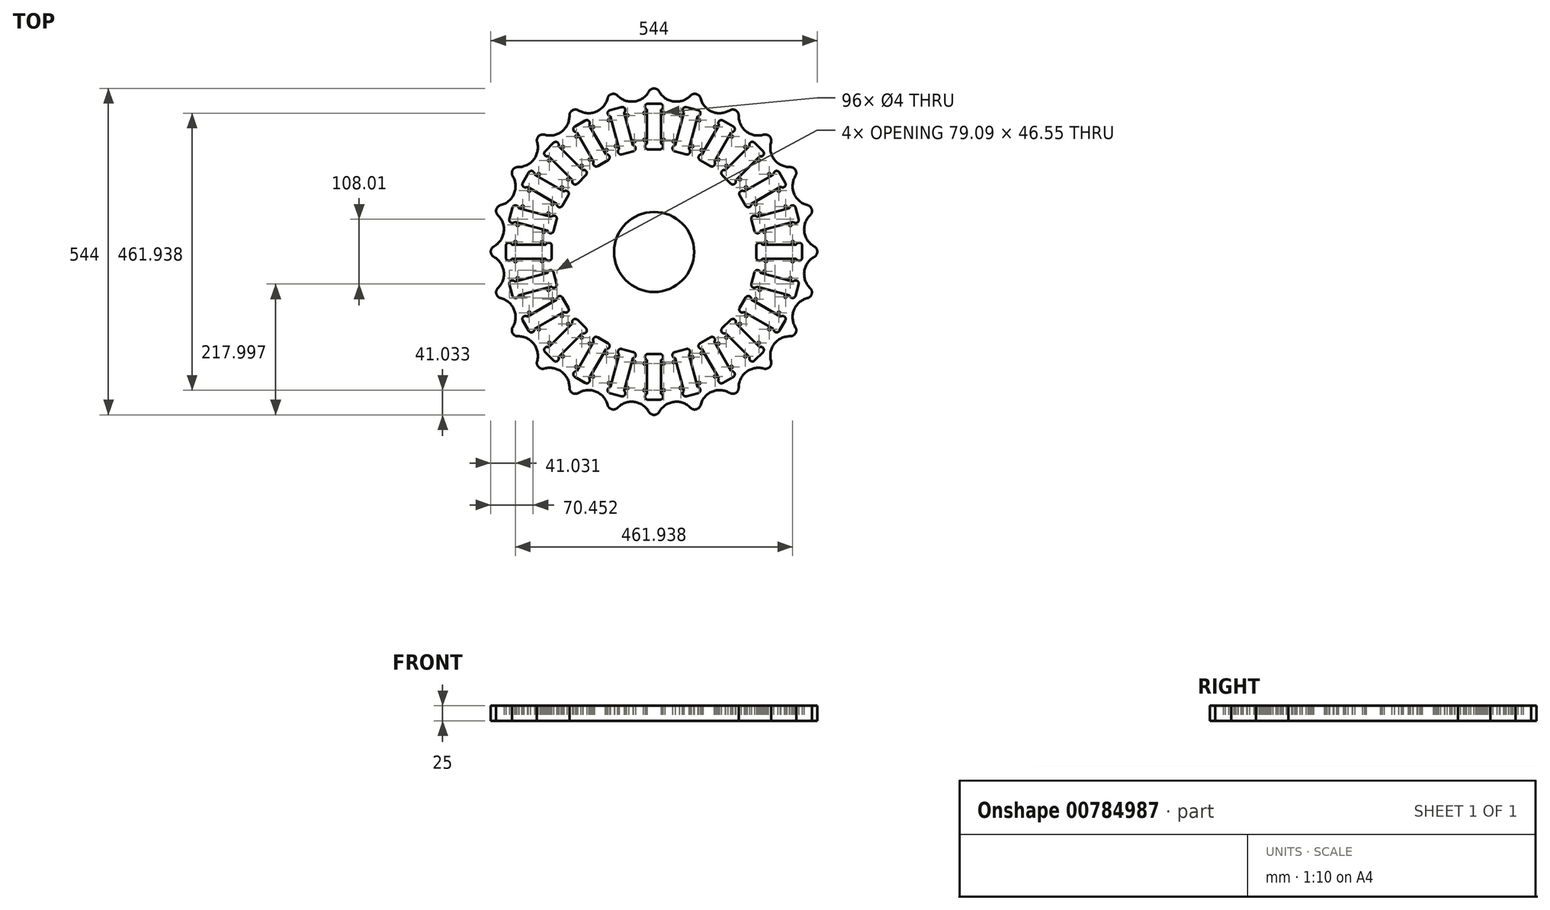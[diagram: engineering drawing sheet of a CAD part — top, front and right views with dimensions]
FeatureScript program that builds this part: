
annotation { "Feature Type Name" : "Feature", "Feature Type Description" : "" }
export const myFeature = defineFeature(function(context is Context, id is Id, definition is map)
    precondition{}
    {
        {
            var Q0;
            Q0=qCreatedBy(makeId("Top.planeOp"),FACE);
            var sketch = newSketch(context, id + "F0", { "sketchPlane" : qUnion([Q0])});
            skCircle(sketch, "E0", {"center": v(0, 0) * mm, "radius": 66.68 * mm});
            skCircle(sketch, "E1", {"center": v(0, 0) * mm, "radius": 35 * mm, "construction": true});
            skArc(sketch, "E2", {"start": v(-21.4, 32.9) * mm, "mid": v(-22.65, 27.02) * mm, "end": v(-16.77, 25.78) * mm});
            skArc(sketch, "E3", {"start": v(16.77, 25.78) * mm, "mid": v(22.65, 27.02) * mm, "end": v(21.4, 32.9) * mm});
            skArc(sketch, "E4", {"start": v(16.77, 25.78) * mm, "mid": v(0, 30.75) * mm, "end": v(-16.77, 25.78) * mm});
            skArc(sketch, "E5", {"start": v(21.4, 32.9) * mm, "mid": v(0, 39.25) * mm, "end": v(-21.4, 32.9) * mm});
            skPoint(sketch, "E6", {"position": v(0, 30.75) * mm});
            skPoint(sketch, "E7", {"position": v(-22.5, 26.8) * mm});
            skPoint(sketch, "E8", {"position": v(22.5, 26.8) * mm});
            skCircle(sketch, "E9", {"center": v(0, 0) * mm, "radius": 22.23 * mm});
            skArc(sketch, "E10.1.0", {"start": v(-17.8, -34.99) * mm, "mid": v(-12.08, -33.12) * mm, "end": v(-13.94, -27.4) * mm});
            skArc(sketch, "E10.1.1", {"start": v(-39.2, 2.08) * mm, "mid": v(-34, -19.62) * mm, "end": v(-17.8, -34.99) * mm});
            skArc(sketch, "E10.1.2", {"start": v(-30.7, 1.63) * mm, "mid": v(-26.63, -15.37) * mm, "end": v(-13.94, -27.4) * mm});
            skArc(sketch, "E10.1.3", {"start": v(-30.7, 1.63) * mm, "mid": v(-34.72, 6.1) * mm, "end": v(-39.2, 2.08) * mm});
            skArc(sketch, "E10.2.0", {"start": v(39.2, 2.08) * mm, "mid": v(34.72, 6.1) * mm, "end": v(30.7, 1.63) * mm});
            skArc(sketch, "E10.2.1", {"start": v(17.8, -34.99) * mm, "mid": v(34, -19.63) * mm, "end": v(39.2, 2.08) * mm});
            skArc(sketch, "E10.2.2", {"start": v(13.94, -27.4) * mm, "mid": v(26.63, -15.38) * mm, "end": v(30.7, 1.63) * mm});
            skArc(sketch, "E10.2.3", {"start": v(13.94, -27.4) * mm, "mid": v(12.08, -33.12) * mm, "end": v(17.8, -34.99) * mm});
            skLineSegment(sketch, "E11", {"start": v(0, 0) * mm, "end": v(0, 283.97) * mm, "construction": true});
            skArc(sketch, "E12", {"start": v(8.75, 267.34) * mm, "mid": v(0, 272.5) * mm, "end": v(-8.75, 267.34) * mm});
            skLineSegment(sketch, "E13", {"start": v(0, 0) * mm, "end": v(37.8, 287.62) * mm, "construction": true});
            skArc(sketch, "E14", {"start": v(8.75, 267.34) * mm, "mid": v(18.9, 256.2) * mm, "end": v(32.96, 250.84) * mm});
            skPoint(sketch, "E15", {"position": v(32.96, 250.84) * mm});
            skArc(sketch, "E16.MirrorC", {"start": v(-8.75, 267.34) * mm, "mid": v(-18.9, 256.2) * mm, "end": v(-32.96, 250.84) * mm});
            skLineSegment(sketch, "E17.MirrorCS", {"start": v(0, 0) * mm, "end": v(-37.8, 287.62) * mm, "construction": true});
            skLineSegment(sketch, "E18", {"start": v(-10, 247.26) * mm, "end": v(0, 247.26) * mm});
            skLineSegment(sketch, "E19", {"start": v(-10, 171.06) * mm, "end": v(0, 171.06) * mm});
            skArc(sketch, "E20", {"start": v(-10, 247.26) * mm, "mid": v(-14.99, 243.15) * mm, "end": v(-11.9, 237.47) * mm});
            skPoint(sketch, "E21", {"position": v(-10, 247.26) * mm});
            skArc(sketch, "E22", {"start": v(-11.9, 180.85) * mm, "mid": v(-14.99, 175.17) * mm, "end": v(-10, 171.06) * mm});
            skPoint(sketch, "E23", {"position": v(-10, 171.06) * mm});
            skLineSegment(sketch, "E24", {"start": v(-11.9, 237.47) * mm, "end": v(-11.9, 180.85) * mm});
            skPoint(sketch, "E25", {"position": v(-15.08, 242.18) * mm});
            skPoint(sketch, "E26", {"position": v(-15.08, 176.14) * mm});
            skLineSegment(sketch, "E27.MirrorCS", {"start": v(10, 247.26) * mm, "end": v(0, 247.26) * mm});
            skArc(sketch, "E28.MirrorCS", {"start": v(10, 247.26) * mm, "mid": v(14.99, 243.15) * mm, "end": v(11.9, 237.47) * mm});
            skLineSegment(sketch, "E29.MirrorCS", {"start": v(11.9, 237.47) * mm, "end": v(11.9, 180.85) * mm});
            skArc(sketch, "E30.MirrorCS", {"start": v(11.9, 180.85) * mm, "mid": v(14.99, 175.17) * mm, "end": v(10, 171.06) * mm});
            skLineSegment(sketch, "E31.MirrorCS", {"start": v(10, 171.06) * mm, "end": v(0, 171.06) * mm});
            skCircle(sketch, "E32", {"center": v(-15.9, 231.47) * mm, "radius": 2 * mm});
            skCircle(sketch, "E33", {"center": v(-15.9, 186.85) * mm, "radius": 2 * mm});
            skCircle(sketch, "E34.MirrorC", {"center": v(15.9, 231.47) * mm, "radius": 2 * mm});
            skCircle(sketch, "E35.MirrorC", {"center": v(15.9, 186.85) * mm, "radius": 2 * mm});
            skCircle(sketch, "E36", {"center": v(0, 0) * mm, "radius": 272.5 * mm, "construction": true});
            skArc(sketch, "E37.1.0", {"start": v(-77.52, 255.98) * mm, "mid": v(-84.43, 242.6) * mm, "end": v(-96.63, 233.78) * mm});
            skArc(sketch, "E37.1.1", {"start": v(-60.6, 260.51) * mm, "mid": v(-47.93, 252.39) * mm, "end": v(-32.96, 250.84) * mm});
            skArc(sketch, "E37.1.2", {"start": v(-60.6, 260.51) * mm, "mid": v(-70.4, 263.23) * mm, "end": v(-77.52, 255.98) * mm});
            skArc(sketch, "E37.1.3", {"start": v(-73.53, 236.26) * mm, "mid": v(-77.28, 231) * mm, "end": v(-72.83, 226.31) * mm});
            skLineSegment(sketch, "E37.1.4", {"start": v(-73.53, 236.26) * mm, "end": v(-63.87, 238.85) * mm});
            skLineSegment(sketch, "E37.1.5", {"start": v(-54.2, 241.44) * mm, "end": v(-63.87, 238.85) * mm});
            skArc(sketch, "E37.1.6", {"start": v(-54.2, 241.44) * mm, "mid": v(-48.33, 238.76) * mm, "end": v(-49.83, 232.48) * mm});
            skLineSegment(sketch, "E37.1.7", {"start": v(-49.83, 232.48) * mm, "end": v(-35.18, 177.79) * mm});
            skLineSegment(sketch, "E37.1.8", {"start": v(-72.83, 226.31) * mm, "end": v(-58.18, 171.62) * mm});
            skArc(sketch, "E37.1.9", {"start": v(-58.18, 171.62) * mm, "mid": v(-59.68, 165.34) * mm, "end": v(-53.8, 162.66) * mm});
            skLineSegment(sketch, "E37.1.10", {"start": v(-53.8, 162.66) * mm, "end": v(-44.14, 165.25) * mm});
            skLineSegment(sketch, "E37.1.11", {"start": v(-34.48, 167.84) * mm, "end": v(-44.14, 165.25) * mm});
            skArc(sketch, "E37.1.12", {"start": v(-35.18, 177.79) * mm, "mid": v(-30.73, 173.1) * mm, "end": v(-34.48, 167.84) * mm});
            skCircle(sketch, "E37.1.13", {"center": v(-32.87, 184.62) * mm, "radius": 2 * mm});
            skCircle(sketch, "E37.1.14", {"center": v(-63.6, 176.38) * mm, "radius": 2 * mm});
            skCircle(sketch, "E37.1.15", {"center": v(-44.41, 227.72) * mm, "radius": 2 * mm});
            skCircle(sketch, "E37.1.16", {"center": v(-75.14, 219.48) * mm, "radius": 2 * mm});
            skArc(sketch, "E37.2.0", {"start": v(-141, 227.21) * mm, "mid": v(-144.21, 212.5) * mm, "end": v(-153.71, 200.83) * mm});
            skArc(sketch, "E37.2.1", {"start": v(-125.84, 235.97) * mm, "mid": v(-111.5, 231.4) * mm, "end": v(-96.63, 233.78) * mm});
            skArc(sketch, "E37.2.2", {"start": v(-125.84, 235.97) * mm, "mid": v(-136, 236.06) * mm, "end": v(-141, 227.21) * mm});
            skArc(sketch, "E37.2.3", {"start": v(-132.04, 209.2) * mm, "mid": v(-134.3, 203.15) * mm, "end": v(-128.8, 199.77) * mm});
            skLineSegment(sketch, "E37.2.4", {"start": v(-132.04, 209.2) * mm, "end": v(-123.38, 214.2) * mm});
            skLineSegment(sketch, "E37.2.5", {"start": v(-114.72, 219.2) * mm, "end": v(-123.38, 214.2) * mm});
            skArc(sketch, "E37.2.6", {"start": v(-114.72, 219.2) * mm, "mid": v(-108.34, 218.14) * mm, "end": v(-108.17, 211.68) * mm});
            skLineSegment(sketch, "E37.2.7", {"start": v(-108.17, 211.68) * mm, "end": v(-79.86, 162.64) * mm});
            skLineSegment(sketch, "E37.2.8", {"start": v(-128.8, 199.77) * mm, "end": v(-100.48, 150.73) * mm});
            skArc(sketch, "E37.2.9", {"start": v(-100.48, 150.73) * mm, "mid": v(-100.31, 144.27) * mm, "end": v(-93.94, 143.2) * mm});
            skLineSegment(sketch, "E37.2.10", {"start": v(-93.94, 143.2) * mm, "end": v(-85.28, 148.2) * mm});
            skLineSegment(sketch, "E37.2.11", {"start": v(-76.62, 153.21) * mm, "end": v(-85.28, 148.2) * mm});
            skArc(sketch, "E37.2.12", {"start": v(-79.86, 162.64) * mm, "mid": v(-74.35, 159.26) * mm, "end": v(-76.62, 153.21) * mm});
            skCircle(sketch, "E37.2.13", {"center": v(-79.4, 169.84) * mm, "radius": 2 * mm});
            skCircle(sketch, "E37.2.14", {"center": v(-106.95, 153.93) * mm, "radius": 2 * mm});
            skCircle(sketch, "E37.2.15", {"center": v(-101.7, 208.48) * mm, "radius": 2 * mm});
            skCircle(sketch, "E37.2.16", {"center": v(-129.26, 192.57) * mm, "radius": 2 * mm});
            skPoint(sketch, "E37.center", {"position": v(0, 0.5) * mm});
            skArc(sketch, "E38.3.3.0", {"start": v(-194.87, 183) * mm, "mid": v(-194.17, 167.96) * mm, "end": v(-200.32, 154.22) * mm});
            skArc(sketch, "E38.4.3.0", {"start": v(-182.5, 195.37) * mm, "mid": v(-167.46, 194.67) * mm, "end": v(-153.71, 200.83) * mm});
            skArc(sketch, "E38.8.3.0", {"start": v(-182.5, 195.37) * mm, "mid": v(-192.33, 192.83) * mm, "end": v(-194.87, 183) * mm});
            skArc(sketch, "E38.12.3.0", {"start": v(-181.56, 167.91) * mm, "mid": v(-182.18, 161.48) * mm, "end": v(-175.98, 159.65) * mm});
            skLineSegment(sketch, "E38.16.3.0", {"start": v(-181.56, 167.91) * mm, "end": v(-174.48, 174.99) * mm});
            skLineSegment(sketch, "E38.19.3.0", {"start": v(-167.41, 182.06) * mm, "end": v(-174.48, 174.99) * mm});
            skArc(sketch, "E38.22.3.0", {"start": v(-167.41, 182.06) * mm, "mid": v(-160.98, 182.68) * mm, "end": v(-159.14, 176.48) * mm});
            skLineSegment(sketch, "E38.26.3.0", {"start": v(-159.14, 176.48) * mm, "end": v(-119.1, 136.45) * mm});
            skLineSegment(sketch, "E38.29.3.0", {"start": v(-175.98, 159.65) * mm, "end": v(-135.94, 119.6) * mm});
            skArc(sketch, "E38.32.3.0", {"start": v(-135.94, 119.6) * mm, "mid": v(-134.1, 113.41) * mm, "end": v(-127.67, 114.03) * mm});
            skLineSegment(sketch, "E38.36.3.0", {"start": v(-127.67, 114.03) * mm, "end": v(-120.6, 121.1) * mm});
            skLineSegment(sketch, "E38.39.3.0", {"start": v(-113.53, 128.18) * mm, "end": v(-120.6, 121.1) * mm});
            skArc(sketch, "E38.42.3.0", {"start": v(-119.1, 136.45) * mm, "mid": v(-112.91, 134.6) * mm, "end": v(-113.53, 128.18) * mm});
            skCircle(sketch, "E38.46.3.0", {"center": v(-120.52, 143.52) * mm, "radius": 2 * mm});
            skCircle(sketch, "E38.48.3.0", {"center": v(-143.02, 121.02) * mm, "radius": 2 * mm});
            skCircle(sketch, "E38.50.3.0", {"center": v(-152.07, 175.07) * mm, "radius": 2 * mm});
            skCircle(sketch, "E38.52.3.0", {"center": v(-174.57, 152.57) * mm, "radius": 2 * mm});
            skArc(sketch, "E38.3.4.0", {"start": v(-235.46, 126.34) * mm, "mid": v(-230.9, 112) * mm, "end": v(-233.28, 97.13) * mm});
            skArc(sketch, "E38.4.4.0", {"start": v(-226.71, 141.5) * mm, "mid": v(-212, 144.72) * mm, "end": v(-200.32, 154.22) * mm});
            skArc(sketch, "E38.8.4.0", {"start": v(-226.71, 141.5) * mm, "mid": v(-235.56, 136.5) * mm, "end": v(-235.46, 126.34) * mm});
            skArc(sketch, "E38.12.4.0", {"start": v(-218.7, 115.22) * mm, "mid": v(-217.63, 108.85) * mm, "end": v(-211.17, 108.68) * mm});
            skLineSegment(sketch, "E38.16.4.0", {"start": v(-218.7, 115.22) * mm, "end": v(-213.7, 123.88) * mm});
            skLineSegment(sketch, "E38.19.4.0", {"start": v(-208.7, 132.54) * mm, "end": v(-213.7, 123.88) * mm});
            skArc(sketch, "E38.22.4.0", {"start": v(-208.7, 132.54) * mm, "mid": v(-202.65, 134.8) * mm, "end": v(-199.27, 129.3) * mm});
            skLineSegment(sketch, "E38.26.4.0", {"start": v(-199.27, 129.3) * mm, "end": v(-150.23, 100.99) * mm});
            skLineSegment(sketch, "E38.29.4.0", {"start": v(-211.17, 108.68) * mm, "end": v(-162.14, 80.36) * mm});
            skArc(sketch, "E38.32.4.0", {"start": v(-162.14, 80.36) * mm, "mid": v(-158.76, 74.86) * mm, "end": v(-152.7, 77.12) * mm});
            skLineSegment(sketch, "E38.36.4.0", {"start": v(-152.7, 77.12) * mm, "end": v(-147.7, 85.78) * mm});
            skLineSegment(sketch, "E38.39.4.0", {"start": v(-142.7, 94.44) * mm, "end": v(-147.7, 85.78) * mm});
            skArc(sketch, "E38.42.4.0", {"start": v(-150.23, 100.99) * mm, "mid": v(-143.77, 100.82) * mm, "end": v(-142.7, 94.44) * mm});
            skCircle(sketch, "E38.46.4.0", {"center": v(-153.43, 107.45) * mm, "radius": 2 * mm});
            skCircle(sketch, "E38.48.4.0", {"center": v(-169.33, 79.9) * mm, "radius": 2 * mm});
            skCircle(sketch, "E38.50.4.0", {"center": v(-192.07, 129.76) * mm, "radius": 2 * mm});
            skCircle(sketch, "E38.52.4.0", {"center": v(-207.98, 102.21) * mm, "radius": 2 * mm});
            skArc(sketch, "E38.3.5.0", {"start": v(-260.01, 61.11) * mm, "mid": v(-251.88, 48.44) * mm, "end": v(-250.34, 33.46) * mm});
            skArc(sketch, "E38.4.5.0", {"start": v(-255.48, 78.02) * mm, "mid": v(-242.1, 84.93) * mm, "end": v(-233.28, 97.13) * mm});
            skArc(sketch, "E38.8.5.0", {"start": v(-255.48, 78.02) * mm, "mid": v(-262.73, 70.9) * mm, "end": v(-260.01, 61.11) * mm});
            skArc(sketch, "E38.12.5.0", {"start": v(-240.94, 54.7) * mm, "mid": v(-238.26, 48.83) * mm, "end": v(-231.98, 50.33) * mm});
            skLineSegment(sketch, "E38.16.5.0", {"start": v(-240.94, 54.7) * mm, "end": v(-238.35, 64.37) * mm});
            skLineSegment(sketch, "E38.19.5.0", {"start": v(-235.76, 74.03) * mm, "end": v(-238.35, 64.37) * mm});
            skArc(sketch, "E38.22.5.0", {"start": v(-235.76, 74.03) * mm, "mid": v(-230.5, 77.78) * mm, "end": v(-225.81, 73.33) * mm});
            skLineSegment(sketch, "E38.26.5.0", {"start": v(-225.81, 73.33) * mm, "end": v(-171.12, 58.68) * mm});
            skLineSegment(sketch, "E38.29.5.0", {"start": v(-231.98, 50.33) * mm, "end": v(-177.28, 35.68) * mm});
            skArc(sketch, "E38.32.5.0", {"start": v(-177.28, 35.68) * mm, "mid": v(-172.6, 31.23) * mm, "end": v(-167.34, 34.98) * mm});
            skLineSegment(sketch, "E38.36.5.0", {"start": v(-167.34, 34.98) * mm, "end": v(-164.75, 44.65) * mm});
            skLineSegment(sketch, "E38.39.5.0", {"start": v(-162.16, 54.3) * mm, "end": v(-164.75, 44.65) * mm});
            skArc(sketch, "E38.42.5.0", {"start": v(-171.12, 58.68) * mm, "mid": v(-164.84, 60.19) * mm, "end": v(-162.16, 54.3) * mm});
            skCircle(sketch, "E38.46.5.0", {"center": v(-175.88, 64.1) * mm, "radius": 2 * mm});
            skCircle(sketch, "E38.48.5.0", {"center": v(-184.11, 33.37) * mm, "radius": 2 * mm});
            skCircle(sketch, "E38.50.5.0", {"center": v(-218.98, 75.65) * mm, "radius": 2 * mm});
            skCircle(sketch, "E38.52.5.0", {"center": v(-227.22, 44.92) * mm, "radius": 2 * mm});
            skArc(sketch, "E38.3.6.0", {"start": v(-266.84, -8.25) * mm, "mid": v(-255.7, -18.39) * mm, "end": v(-250.34, -32.46) * mm});
            skArc(sketch, "E38.4.6.0", {"start": v(-266.84, 9.25) * mm, "mid": v(-255.7, 19.4) * mm, "end": v(-250.34, 33.46) * mm});
            skArc(sketch, "E38.8.6.0", {"start": v(-266.84, 9.25) * mm, "mid": v(-272, 0.5) * mm, "end": v(-266.84, -8.25) * mm});
            skArc(sketch, "E38.12.6.0", {"start": v(-246.76, -9.5) * mm, "mid": v(-242.65, -14.49) * mm, "end": v(-236.97, -11.4) * mm});
            skLineSegment(sketch, "E38.16.6.0", {"start": v(-246.76, -9.5) * mm, "end": v(-246.76, 0.5) * mm});
            skLineSegment(sketch, "E38.19.6.0", {"start": v(-246.76, 10.5) * mm, "end": v(-246.76, 0.5) * mm});
            skArc(sketch, "E38.22.6.0", {"start": v(-246.76, 10.5) * mm, "mid": v(-242.65, 15.49) * mm, "end": v(-236.97, 12.4) * mm});
            skLineSegment(sketch, "E38.26.6.0", {"start": v(-236.97, 12.4) * mm, "end": v(-180.35, 12.4) * mm});
            skLineSegment(sketch, "E38.29.6.0", {"start": v(-236.97, -11.4) * mm, "end": v(-180.35, -11.4) * mm});
            skArc(sketch, "E38.32.6.0", {"start": v(-180.35, -11.4) * mm, "mid": v(-174.67, -14.49) * mm, "end": v(-170.56, -9.5) * mm});
            skLineSegment(sketch, "E38.36.6.0", {"start": v(-170.56, -9.5) * mm, "end": v(-170.56, 0.5) * mm});
            skLineSegment(sketch, "E38.39.6.0", {"start": v(-170.56, 10.5) * mm, "end": v(-170.56, 0.5) * mm});
            skArc(sketch, "E38.42.6.0", {"start": v(-180.35, 12.4) * mm, "mid": v(-174.67, 15.49) * mm, "end": v(-170.56, 10.5) * mm});
            skCircle(sketch, "E38.46.6.0", {"center": v(-186.35, 16.4) * mm, "radius": 2 * mm});
            skCircle(sketch, "E38.48.6.0", {"center": v(-186.35, -15.4) * mm, "radius": 2 * mm});
            skCircle(sketch, "E38.50.6.0", {"center": v(-230.97, 16.4) * mm, "radius": 2 * mm});
            skCircle(sketch, "E38.52.6.0", {"center": v(-230.97, -15.4) * mm, "radius": 2 * mm});
            skArc(sketch, "E38.3.7.0", {"start": v(-255.48, -77.01) * mm, "mid": v(-242.1, -83.93) * mm, "end": v(-233.28, -96.13) * mm});
            skArc(sketch, "E38.4.7.0", {"start": v(-260.01, -60.1) * mm, "mid": v(-251.88, -47.43) * mm, "end": v(-250.34, -32.46) * mm});
            skArc(sketch, "E38.8.7.0", {"start": v(-260.01, -60.1) * mm, "mid": v(-262.73, -69.9) * mm, "end": v(-255.48, -77.01) * mm});
            skArc(sketch, "E38.12.7.0", {"start": v(-235.76, -73.02) * mm, "mid": v(-230.5, -76.78) * mm, "end": v(-225.81, -72.33) * mm});
            skLineSegment(sketch, "E38.16.7.0", {"start": v(-235.76, -73.02) * mm, "end": v(-238.35, -63.36) * mm});
            skLineSegment(sketch, "E38.19.7.0", {"start": v(-240.94, -53.7) * mm, "end": v(-238.35, -63.36) * mm});
            skArc(sketch, "E38.22.7.0", {"start": v(-240.94, -53.7) * mm, "mid": v(-238.26, -47.82) * mm, "end": v(-231.98, -49.33) * mm});
            skLineSegment(sketch, "E38.26.7.0", {"start": v(-231.98, -49.33) * mm, "end": v(-177.28, -34.68) * mm});
            skLineSegment(sketch, "E38.29.7.0", {"start": v(-225.81, -72.33) * mm, "end": v(-171.12, -57.68) * mm});
            skArc(sketch, "E38.32.7.0", {"start": v(-171.12, -57.68) * mm, "mid": v(-164.84, -59.18) * mm, "end": v(-162.16, -53.3) * mm});
            skLineSegment(sketch, "E38.36.7.0", {"start": v(-162.16, -53.3) * mm, "end": v(-164.75, -43.64) * mm});
            skLineSegment(sketch, "E38.39.7.0", {"start": v(-167.34, -33.98) * mm, "end": v(-164.75, -43.64) * mm});
            skArc(sketch, "E38.42.7.0", {"start": v(-177.28, -34.68) * mm, "mid": v(-172.6, -30.23) * mm, "end": v(-167.34, -33.98) * mm});
            skCircle(sketch, "E38.46.7.0", {"center": v(-184.11, -32.36) * mm, "radius": 2 * mm});
            skCircle(sketch, "E38.48.7.0", {"center": v(-175.88, -63.1) * mm, "radius": 2 * mm});
            skCircle(sketch, "E38.50.7.0", {"center": v(-227.22, -43.91) * mm, "radius": 2 * mm});
            skCircle(sketch, "E38.52.7.0", {"center": v(-218.98, -74.64) * mm, "radius": 2 * mm});
            skArc(sketch, "E38.3.8.0", {"start": v(-226.71, -140.5) * mm, "mid": v(-212, -143.71) * mm, "end": v(-200.32, -153.21) * mm});
            skArc(sketch, "E38.4.8.0", {"start": v(-235.46, -125.34) * mm, "mid": v(-230.9, -111) * mm, "end": v(-233.28, -96.13) * mm});
            skArc(sketch, "E38.8.8.0", {"start": v(-235.46, -125.34) * mm, "mid": v(-235.56, -135.5) * mm, "end": v(-226.71, -140.5) * mm});
            skArc(sketch, "E38.12.8.0", {"start": v(-208.7, -131.54) * mm, "mid": v(-202.65, -133.8) * mm, "end": v(-199.27, -128.3) * mm});
            skLineSegment(sketch, "E38.16.8.0", {"start": v(-208.7, -131.54) * mm, "end": v(-213.7, -122.88) * mm});
            skLineSegment(sketch, "E38.19.8.0", {"start": v(-218.7, -114.22) * mm, "end": v(-213.7, -122.88) * mm});
            skArc(sketch, "E38.22.8.0", {"start": v(-218.7, -114.22) * mm, "mid": v(-217.63, -107.84) * mm, "end": v(-211.17, -107.67) * mm});
            skLineSegment(sketch, "E38.26.8.0", {"start": v(-211.17, -107.67) * mm, "end": v(-162.14, -79.36) * mm});
            skLineSegment(sketch, "E38.29.8.0", {"start": v(-199.27, -128.3) * mm, "end": v(-150.23, -99.98) * mm});
            skArc(sketch, "E38.32.8.0", {"start": v(-150.23, -99.98) * mm, "mid": v(-143.77, -99.81) * mm, "end": v(-142.7, -93.44) * mm});
            skLineSegment(sketch, "E38.36.8.0", {"start": v(-142.7, -93.44) * mm, "end": v(-147.7, -84.78) * mm});
            skLineSegment(sketch, "E38.39.8.0", {"start": v(-152.7, -76.12) * mm, "end": v(-147.7, -84.78) * mm});
            skArc(sketch, "E38.42.8.0", {"start": v(-162.14, -79.36) * mm, "mid": v(-158.76, -73.85) * mm, "end": v(-152.7, -76.12) * mm});
            skCircle(sketch, "E38.46.8.0", {"center": v(-169.33, -78.9) * mm, "radius": 2 * mm});
            skCircle(sketch, "E38.48.8.0", {"center": v(-153.43, -106.45) * mm, "radius": 2 * mm});
            skCircle(sketch, "E38.50.8.0", {"center": v(-207.98, -101.2) * mm, "radius": 2 * mm});
            skCircle(sketch, "E38.52.8.0", {"center": v(-192.07, -128.76) * mm, "radius": 2 * mm});
            skArc(sketch, "E38.3.9.0", {"start": v(-182.5, -194.37) * mm, "mid": v(-167.46, -193.67) * mm, "end": v(-153.71, -199.82) * mm});
            skArc(sketch, "E38.4.9.0", {"start": v(-194.87, -182) * mm, "mid": v(-194.17, -166.95) * mm, "end": v(-200.32, -153.21) * mm});
            skArc(sketch, "E38.8.9.0", {"start": v(-194.87, -182) * mm, "mid": v(-192.33, -191.83) * mm, "end": v(-182.5, -194.37) * mm});
            skArc(sketch, "E38.12.9.0", {"start": v(-167.41, -181.05) * mm, "mid": v(-160.98, -181.67) * mm, "end": v(-159.14, -175.48) * mm});
            skLineSegment(sketch, "E38.16.9.0", {"start": v(-167.41, -181.05) * mm, "end": v(-174.48, -173.98) * mm});
            skLineSegment(sketch, "E38.19.9.0", {"start": v(-181.56, -166.91) * mm, "end": v(-174.48, -173.98) * mm});
            skArc(sketch, "E38.22.9.0", {"start": v(-181.56, -166.91) * mm, "mid": v(-182.18, -160.48) * mm, "end": v(-175.98, -158.64) * mm});
            skLineSegment(sketch, "E38.26.9.0", {"start": v(-175.98, -158.64) * mm, "end": v(-135.94, -118.6) * mm});
            skLineSegment(sketch, "E38.29.9.0", {"start": v(-159.14, -175.48) * mm, "end": v(-119.1, -135.44) * mm});
            skArc(sketch, "E38.32.9.0", {"start": v(-119.1, -135.44) * mm, "mid": v(-112.91, -133.6) * mm, "end": v(-113.53, -127.17) * mm});
            skLineSegment(sketch, "E38.36.9.0", {"start": v(-113.53, -127.17) * mm, "end": v(-120.6, -120.1) * mm});
            skLineSegment(sketch, "E38.39.9.0", {"start": v(-127.67, -113.03) * mm, "end": v(-120.6, -120.1) * mm});
            skArc(sketch, "E38.42.9.0", {"start": v(-135.94, -118.6) * mm, "mid": v(-134.1, -112.4) * mm, "end": v(-127.67, -113.03) * mm});
            skCircle(sketch, "E38.46.9.0", {"center": v(-143.02, -120.02) * mm, "radius": 2 * mm});
            skCircle(sketch, "E38.48.9.0", {"center": v(-120.52, -142.51) * mm, "radius": 2 * mm});
            skCircle(sketch, "E38.50.9.0", {"center": v(-174.57, -151.57) * mm, "radius": 2 * mm});
            skCircle(sketch, "E38.52.9.0", {"center": v(-152.07, -174.07) * mm, "radius": 2 * mm});
            skArc(sketch, "E38.3.10.0", {"start": v(-125.84, -234.96) * mm, "mid": v(-111.5, -230.4) * mm, "end": v(-96.63, -232.78) * mm});
            skArc(sketch, "E38.4.10.0", {"start": v(-141, -226.21) * mm, "mid": v(-144.21, -211.5) * mm, "end": v(-153.71, -199.82) * mm});
            skArc(sketch, "E38.8.10.0", {"start": v(-141, -226.21) * mm, "mid": v(-136, -235.06) * mm, "end": v(-125.84, -234.96) * mm});
            skArc(sketch, "E38.12.10.0", {"start": v(-114.72, -218.2) * mm, "mid": v(-108.34, -217.13) * mm, "end": v(-108.17, -210.67) * mm});
            skLineSegment(sketch, "E38.16.10.0", {"start": v(-114.72, -218.2) * mm, "end": v(-123.38, -213.2) * mm});
            skLineSegment(sketch, "E38.19.10.0", {"start": v(-132.04, -208.2) * mm, "end": v(-123.38, -213.2) * mm});
            skArc(sketch, "E38.22.10.0", {"start": v(-132.04, -208.2) * mm, "mid": v(-134.3, -202.14) * mm, "end": v(-128.8, -198.77) * mm});
            skLineSegment(sketch, "E38.26.10.0", {"start": v(-128.8, -198.77) * mm, "end": v(-100.48, -149.73) * mm});
            skLineSegment(sketch, "E38.29.10.0", {"start": v(-108.17, -210.67) * mm, "end": v(-79.86, -161.64) * mm});
            skArc(sketch, "E38.32.10.0", {"start": v(-79.86, -161.64) * mm, "mid": v(-74.35, -158.26) * mm, "end": v(-76.62, -152.2) * mm});
            skLineSegment(sketch, "E38.36.10.0", {"start": v(-76.62, -152.2) * mm, "end": v(-85.28, -147.2) * mm});
            skLineSegment(sketch, "E38.39.10.0", {"start": v(-93.94, -142.2) * mm, "end": v(-85.28, -147.2) * mm});
            skArc(sketch, "E38.42.10.0", {"start": v(-100.48, -149.73) * mm, "mid": v(-100.31, -143.27) * mm, "end": v(-93.94, -142.2) * mm});
            skCircle(sketch, "E38.46.10.0", {"center": v(-106.95, -152.93) * mm, "radius": 2 * mm});
            skCircle(sketch, "E38.48.10.0", {"center": v(-79.4, -168.83) * mm, "radius": 2 * mm});
            skCircle(sketch, "E38.50.10.0", {"center": v(-129.26, -191.57) * mm, "radius": 2 * mm});
            skCircle(sketch, "E38.52.10.0", {"center": v(-101.7, -207.48) * mm, "radius": 2 * mm});
            skArc(sketch, "E38.3.11.0", {"start": v(-60.6, -259.5) * mm, "mid": v(-47.93, -251.38) * mm, "end": v(-32.96, -249.84) * mm});
            skArc(sketch, "E38.4.11.0", {"start": v(-77.52, -254.98) * mm, "mid": v(-84.43, -241.6) * mm, "end": v(-96.63, -232.78) * mm});
            skArc(sketch, "E38.8.11.0", {"start": v(-77.52, -254.98) * mm, "mid": v(-70.4, -262.23) * mm, "end": v(-60.6, -259.5) * mm});
            skArc(sketch, "E38.12.11.0", {"start": v(-54.2, -240.44) * mm, "mid": v(-48.33, -237.76) * mm, "end": v(-49.83, -231.47) * mm});
            skLineSegment(sketch, "E38.16.11.0", {"start": v(-54.2, -240.44) * mm, "end": v(-63.87, -237.85) * mm});
            skLineSegment(sketch, "E38.19.11.0", {"start": v(-73.53, -235.26) * mm, "end": v(-63.87, -237.85) * mm});
            skArc(sketch, "E38.22.11.0", {"start": v(-73.53, -235.26) * mm, "mid": v(-77.28, -230) * mm, "end": v(-72.83, -225.31) * mm});
            skLineSegment(sketch, "E38.26.11.0", {"start": v(-72.83, -225.31) * mm, "end": v(-58.18, -170.62) * mm});
            skLineSegment(sketch, "E38.29.11.0", {"start": v(-49.83, -231.47) * mm, "end": v(-35.18, -176.78) * mm});
            skArc(sketch, "E38.32.11.0", {"start": v(-35.18, -176.78) * mm, "mid": v(-30.73, -172.1) * mm, "end": v(-34.48, -166.83) * mm});
            skLineSegment(sketch, "E38.36.11.0", {"start": v(-34.48, -166.83) * mm, "end": v(-44.14, -164.25) * mm});
            skLineSegment(sketch, "E38.39.11.0", {"start": v(-53.8, -161.66) * mm, "end": v(-44.14, -164.25) * mm});
            skArc(sketch, "E38.42.11.0", {"start": v(-58.18, -170.62) * mm, "mid": v(-59.68, -164.34) * mm, "end": v(-53.8, -161.66) * mm});
            skCircle(sketch, "E38.46.11.0", {"center": v(-63.6, -175.38) * mm, "radius": 2 * mm});
            skCircle(sketch, "E38.48.11.0", {"center": v(-32.87, -183.61) * mm, "radius": 2 * mm});
            skCircle(sketch, "E38.50.11.0", {"center": v(-75.14, -218.48) * mm, "radius": 2 * mm});
            skCircle(sketch, "E38.52.11.0", {"center": v(-44.41, -226.71) * mm, "radius": 2 * mm});
            skArc(sketch, "E38.3.12.0", {"start": v(8.75, -266.34) * mm, "mid": v(18.9, -255.2) * mm, "end": v(32.96, -249.84) * mm});
            skArc(sketch, "E38.4.12.0", {"start": v(-8.75, -266.34) * mm, "mid": v(-18.9, -255.2) * mm, "end": v(-32.96, -249.84) * mm});
            skArc(sketch, "E38.8.12.0", {"start": v(-8.75, -266.34) * mm, "mid": v(0, -271.5) * mm, "end": v(8.75, -266.34) * mm});
            skArc(sketch, "E38.12.12.0", {"start": v(10, -246.26) * mm, "mid": v(14.99, -242.15) * mm, "end": v(11.9, -236.47) * mm});
            skLineSegment(sketch, "E38.16.12.0", {"start": v(10, -246.26) * mm, "end": v(0, -246.26) * mm});
            skLineSegment(sketch, "E38.19.12.0", {"start": v(-10, -246.26) * mm, "end": v(0, -246.26) * mm});
            skArc(sketch, "E38.22.12.0", {"start": v(-10, -246.26) * mm, "mid": v(-14.99, -242.15) * mm, "end": v(-11.9, -236.47) * mm});
            skLineSegment(sketch, "E38.26.12.0", {"start": v(-11.9, -236.47) * mm, "end": v(-11.9, -179.85) * mm});
            skLineSegment(sketch, "E38.29.12.0", {"start": v(11.9, -236.47) * mm, "end": v(11.9, -179.85) * mm});
            skArc(sketch, "E38.32.12.0", {"start": v(11.9, -179.85) * mm, "mid": v(14.99, -174.17) * mm, "end": v(10, -170.06) * mm});
            skLineSegment(sketch, "E38.36.12.0", {"start": v(10, -170.06) * mm, "end": v(0, -170.06) * mm});
            skLineSegment(sketch, "E38.39.12.0", {"start": v(-10, -170.06) * mm, "end": v(0, -170.06) * mm});
            skArc(sketch, "E38.42.12.0", {"start": v(-11.9, -179.85) * mm, "mid": v(-14.99, -174.17) * mm, "end": v(-10, -170.06) * mm});
            skCircle(sketch, "E38.46.12.0", {"center": v(-15.9, -185.85) * mm, "radius": 2 * mm});
            skCircle(sketch, "E38.48.12.0", {"center": v(15.9, -185.85) * mm, "radius": 2 * mm});
            skCircle(sketch, "E38.50.12.0", {"center": v(-15.9, -230.47) * mm, "radius": 2 * mm});
            skCircle(sketch, "E38.52.12.0", {"center": v(15.9, -230.47) * mm, "radius": 2 * mm});
            skArc(sketch, "E38.3.13.0", {"start": v(77.52, -254.98) * mm, "mid": v(84.43, -241.6) * mm, "end": v(96.63, -232.78) * mm});
            skArc(sketch, "E38.4.13.0", {"start": v(60.6, -259.5) * mm, "mid": v(47.93, -251.38) * mm, "end": v(32.96, -249.84) * mm});
            skArc(sketch, "E38.8.13.0", {"start": v(60.6, -259.5) * mm, "mid": v(70.4, -262.23) * mm, "end": v(77.52, -254.98) * mm});
            skArc(sketch, "E38.12.13.0", {"start": v(73.53, -235.26) * mm, "mid": v(77.28, -230) * mm, "end": v(72.83, -225.31) * mm});
            skLineSegment(sketch, "E38.16.13.0", {"start": v(73.53, -235.26) * mm, "end": v(63.87, -237.85) * mm});
            skLineSegment(sketch, "E38.19.13.0", {"start": v(54.2, -240.44) * mm, "end": v(63.87, -237.85) * mm});
            skArc(sketch, "E38.22.13.0", {"start": v(54.2, -240.44) * mm, "mid": v(48.33, -237.76) * mm, "end": v(49.83, -231.47) * mm});
            skLineSegment(sketch, "E38.26.13.0", {"start": v(49.83, -231.47) * mm, "end": v(35.18, -176.78) * mm});
            skLineSegment(sketch, "E38.29.13.0", {"start": v(72.83, -225.31) * mm, "end": v(58.18, -170.62) * mm});
            skArc(sketch, "E38.32.13.0", {"start": v(58.18, -170.62) * mm, "mid": v(59.68, -164.34) * mm, "end": v(53.8, -161.66) * mm});
            skLineSegment(sketch, "E38.36.13.0", {"start": v(53.8, -161.66) * mm, "end": v(44.14, -164.25) * mm});
            skLineSegment(sketch, "E38.39.13.0", {"start": v(34.48, -166.83) * mm, "end": v(44.14, -164.25) * mm});
            skArc(sketch, "E38.42.13.0", {"start": v(35.18, -176.78) * mm, "mid": v(30.73, -172.1) * mm, "end": v(34.48, -166.83) * mm});
            skCircle(sketch, "E38.46.13.0", {"center": v(32.87, -183.61) * mm, "radius": 2 * mm});
            skCircle(sketch, "E38.48.13.0", {"center": v(63.6, -175.38) * mm, "radius": 2 * mm});
            skCircle(sketch, "E38.50.13.0", {"center": v(44.41, -226.71) * mm, "radius": 2 * mm});
            skCircle(sketch, "E38.52.13.0", {"center": v(75.14, -218.48) * mm, "radius": 2 * mm});
            skArc(sketch, "E38.3.14.0", {"start": v(141, -226.21) * mm, "mid": v(144.21, -211.5) * mm, "end": v(153.71, -199.82) * mm});
            skArc(sketch, "E38.4.14.0", {"start": v(125.84, -234.96) * mm, "mid": v(111.5, -230.4) * mm, "end": v(96.63, -232.78) * mm});
            skArc(sketch, "E38.8.14.0", {"start": v(125.84, -234.96) * mm, "mid": v(136, -235.06) * mm, "end": v(141, -226.21) * mm});
            skArc(sketch, "E38.12.14.0", {"start": v(132.04, -208.2) * mm, "mid": v(134.3, -202.14) * mm, "end": v(128.8, -198.77) * mm});
            skLineSegment(sketch, "E38.16.14.0", {"start": v(132.04, -208.2) * mm, "end": v(123.38, -213.2) * mm});
            skLineSegment(sketch, "E38.19.14.0", {"start": v(114.72, -218.2) * mm, "end": v(123.38, -213.2) * mm});
            skArc(sketch, "E38.22.14.0", {"start": v(114.72, -218.2) * mm, "mid": v(108.34, -217.13) * mm, "end": v(108.17, -210.67) * mm});
            skLineSegment(sketch, "E38.26.14.0", {"start": v(108.17, -210.67) * mm, "end": v(79.86, -161.64) * mm});
            skLineSegment(sketch, "E38.29.14.0", {"start": v(128.8, -198.77) * mm, "end": v(100.48, -149.73) * mm});
            skArc(sketch, "E38.32.14.0", {"start": v(100.48, -149.73) * mm, "mid": v(100.31, -143.27) * mm, "end": v(93.94, -142.2) * mm});
            skLineSegment(sketch, "E38.36.14.0", {"start": v(93.94, -142.2) * mm, "end": v(85.28, -147.2) * mm});
            skLineSegment(sketch, "E38.39.14.0", {"start": v(76.62, -152.2) * mm, "end": v(85.28, -147.2) * mm});
            skArc(sketch, "E38.42.14.0", {"start": v(79.86, -161.64) * mm, "mid": v(74.35, -158.26) * mm, "end": v(76.62, -152.2) * mm});
            skCircle(sketch, "E38.46.14.0", {"center": v(79.4, -168.83) * mm, "radius": 2 * mm});
            skCircle(sketch, "E38.48.14.0", {"center": v(106.95, -152.93) * mm, "radius": 2 * mm});
            skCircle(sketch, "E38.50.14.0", {"center": v(101.7, -207.48) * mm, "radius": 2 * mm});
            skCircle(sketch, "E38.52.14.0", {"center": v(129.26, -191.57) * mm, "radius": 2 * mm});
            skArc(sketch, "E38.3.15.0", {"start": v(194.87, -182) * mm, "mid": v(194.17, -166.95) * mm, "end": v(200.32, -153.21) * mm});
            skArc(sketch, "E38.4.15.0", {"start": v(182.5, -194.37) * mm, "mid": v(167.46, -193.67) * mm, "end": v(153.71, -199.82) * mm});
            skArc(sketch, "E38.8.15.0", {"start": v(182.5, -194.37) * mm, "mid": v(192.33, -191.83) * mm, "end": v(194.87, -182) * mm});
            skArc(sketch, "E38.12.15.0", {"start": v(181.56, -166.91) * mm, "mid": v(182.18, -160.48) * mm, "end": v(175.98, -158.64) * mm});
            skLineSegment(sketch, "E38.16.15.0", {"start": v(181.56, -166.91) * mm, "end": v(174.48, -173.98) * mm});
            skLineSegment(sketch, "E38.19.15.0", {"start": v(167.41, -181.05) * mm, "end": v(174.48, -173.98) * mm});
            skArc(sketch, "E38.22.15.0", {"start": v(167.41, -181.05) * mm, "mid": v(160.98, -181.67) * mm, "end": v(159.14, -175.48) * mm});
            skLineSegment(sketch, "E38.26.15.0", {"start": v(159.14, -175.48) * mm, "end": v(119.1, -135.44) * mm});
            skLineSegment(sketch, "E38.29.15.0", {"start": v(175.98, -158.64) * mm, "end": v(135.94, -118.6) * mm});
            skArc(sketch, "E38.32.15.0", {"start": v(135.94, -118.6) * mm, "mid": v(134.1, -112.4) * mm, "end": v(127.67, -113.03) * mm});
            skLineSegment(sketch, "E38.36.15.0", {"start": v(127.67, -113.03) * mm, "end": v(120.6, -120.1) * mm});
            skLineSegment(sketch, "E38.39.15.0", {"start": v(113.53, -127.17) * mm, "end": v(120.6, -120.1) * mm});
            skArc(sketch, "E38.42.15.0", {"start": v(119.1, -135.44) * mm, "mid": v(112.91, -133.6) * mm, "end": v(113.53, -127.17) * mm});
            skCircle(sketch, "E38.46.15.0", {"center": v(120.52, -142.51) * mm, "radius": 2 * mm});
            skCircle(sketch, "E38.48.15.0", {"center": v(143.02, -120.02) * mm, "radius": 2 * mm});
            skCircle(sketch, "E38.50.15.0", {"center": v(152.07, -174.07) * mm, "radius": 2 * mm});
            skCircle(sketch, "E38.52.15.0", {"center": v(174.57, -151.57) * mm, "radius": 2 * mm});
            skArc(sketch, "E38.3.16.0", {"start": v(235.46, -125.34) * mm, "mid": v(230.9, -111) * mm, "end": v(233.28, -96.13) * mm});
            skArc(sketch, "E38.4.16.0", {"start": v(226.71, -140.5) * mm, "mid": v(212, -143.71) * mm, "end": v(200.32, -153.21) * mm});
            skArc(sketch, "E38.8.16.0", {"start": v(226.71, -140.5) * mm, "mid": v(235.56, -135.5) * mm, "end": v(235.46, -125.34) * mm});
            skArc(sketch, "E38.12.16.0", {"start": v(218.7, -114.22) * mm, "mid": v(217.63, -107.84) * mm, "end": v(211.17, -107.67) * mm});
            skLineSegment(sketch, "E38.16.16.0", {"start": v(218.7, -114.22) * mm, "end": v(213.7, -122.88) * mm});
            skLineSegment(sketch, "E38.19.16.0", {"start": v(208.7, -131.54) * mm, "end": v(213.7, -122.88) * mm});
            skArc(sketch, "E38.22.16.0", {"start": v(208.7, -131.54) * mm, "mid": v(202.65, -133.8) * mm, "end": v(199.27, -128.3) * mm});
            skLineSegment(sketch, "E38.26.16.0", {"start": v(199.27, -128.3) * mm, "end": v(150.23, -99.98) * mm});
            skLineSegment(sketch, "E38.29.16.0", {"start": v(211.17, -107.67) * mm, "end": v(162.14, -79.36) * mm});
            skArc(sketch, "E38.32.16.0", {"start": v(162.14, -79.36) * mm, "mid": v(158.76, -73.85) * mm, "end": v(152.7, -76.12) * mm});
            skLineSegment(sketch, "E38.36.16.0", {"start": v(152.7, -76.12) * mm, "end": v(147.7, -84.78) * mm});
            skLineSegment(sketch, "E38.39.16.0", {"start": v(142.7, -93.44) * mm, "end": v(147.7, -84.78) * mm});
            skArc(sketch, "E38.42.16.0", {"start": v(150.23, -99.98) * mm, "mid": v(143.77, -99.81) * mm, "end": v(142.7, -93.44) * mm});
            skCircle(sketch, "E38.46.16.0", {"center": v(153.43, -106.45) * mm, "radius": 2 * mm});
            skCircle(sketch, "E38.48.16.0", {"center": v(169.33, -78.9) * mm, "radius": 2 * mm});
            skCircle(sketch, "E38.50.16.0", {"center": v(192.07, -128.76) * mm, "radius": 2 * mm});
            skCircle(sketch, "E38.52.16.0", {"center": v(207.98, -101.2) * mm, "radius": 2 * mm});
            skArc(sketch, "E38.3.17.0", {"start": v(260.01, -60.1) * mm, "mid": v(251.88, -47.43) * mm, "end": v(250.34, -32.46) * mm});
            skArc(sketch, "E38.4.17.0", {"start": v(255.48, -77.01) * mm, "mid": v(242.1, -83.93) * mm, "end": v(233.28, -96.13) * mm});
            skArc(sketch, "E38.8.17.0", {"start": v(255.48, -77.01) * mm, "mid": v(262.73, -69.9) * mm, "end": v(260.01, -60.1) * mm});
            skArc(sketch, "E38.12.17.0", {"start": v(240.94, -53.7) * mm, "mid": v(238.26, -47.82) * mm, "end": v(231.98, -49.33) * mm});
            skLineSegment(sketch, "E38.16.17.0", {"start": v(240.94, -53.7) * mm, "end": v(238.35, -63.36) * mm});
            skLineSegment(sketch, "E38.19.17.0", {"start": v(235.76, -73.02) * mm, "end": v(238.35, -63.36) * mm});
            skArc(sketch, "E38.22.17.0", {"start": v(235.76, -73.02) * mm, "mid": v(230.5, -76.78) * mm, "end": v(225.81, -72.33) * mm});
            skLineSegment(sketch, "E38.26.17.0", {"start": v(225.81, -72.33) * mm, "end": v(171.12, -57.68) * mm});
            skLineSegment(sketch, "E38.29.17.0", {"start": v(231.98, -49.33) * mm, "end": v(177.28, -34.68) * mm});
            skArc(sketch, "E38.32.17.0", {"start": v(177.28, -34.68) * mm, "mid": v(172.6, -30.23) * mm, "end": v(167.34, -33.98) * mm});
            skLineSegment(sketch, "E38.36.17.0", {"start": v(167.34, -33.98) * mm, "end": v(164.75, -43.64) * mm});
            skLineSegment(sketch, "E38.39.17.0", {"start": v(162.16, -53.3) * mm, "end": v(164.75, -43.64) * mm});
            skArc(sketch, "E38.42.17.0", {"start": v(171.12, -57.68) * mm, "mid": v(164.84, -59.18) * mm, "end": v(162.16, -53.3) * mm});
            skCircle(sketch, "E38.46.17.0", {"center": v(175.88, -63.1) * mm, "radius": 2 * mm});
            skCircle(sketch, "E38.48.17.0", {"center": v(184.11, -32.36) * mm, "radius": 2 * mm});
            skCircle(sketch, "E38.50.17.0", {"center": v(218.98, -74.64) * mm, "radius": 2 * mm});
            skCircle(sketch, "E38.52.17.0", {"center": v(227.22, -43.91) * mm, "radius": 2 * mm});
            skArc(sketch, "E38.3.18.0", {"start": v(266.84, 9.25) * mm, "mid": v(255.7, 19.4) * mm, "end": v(250.34, 33.46) * mm});
            skArc(sketch, "E38.4.18.0", {"start": v(266.84, -8.25) * mm, "mid": v(255.7, -18.39) * mm, "end": v(250.34, -32.46) * mm});
            skArc(sketch, "E38.8.18.0", {"start": v(266.84, -8.25) * mm, "mid": v(272, 0.5) * mm, "end": v(266.84, 9.25) * mm});
            skArc(sketch, "E38.12.18.0", {"start": v(246.76, 10.5) * mm, "mid": v(242.65, 15.49) * mm, "end": v(236.97, 12.4) * mm});
            skLineSegment(sketch, "E38.16.18.0", {"start": v(246.76, 10.5) * mm, "end": v(246.76, 0.5) * mm});
            skLineSegment(sketch, "E38.19.18.0", {"start": v(246.76, -9.5) * mm, "end": v(246.76, 0.5) * mm});
            skArc(sketch, "E38.22.18.0", {"start": v(246.76, -9.5) * mm, "mid": v(242.65, -14.49) * mm, "end": v(236.97, -11.4) * mm});
            skLineSegment(sketch, "E38.26.18.0", {"start": v(236.97, -11.4) * mm, "end": v(180.35, -11.4) * mm});
            skLineSegment(sketch, "E38.29.18.0", {"start": v(236.97, 12.4) * mm, "end": v(180.35, 12.4) * mm});
            skArc(sketch, "E38.32.18.0", {"start": v(180.35, 12.4) * mm, "mid": v(174.67, 15.49) * mm, "end": v(170.56, 10.5) * mm});
            skLineSegment(sketch, "E38.36.18.0", {"start": v(170.56, 10.5) * mm, "end": v(170.56, 0.5) * mm});
            skLineSegment(sketch, "E38.39.18.0", {"start": v(170.56, -9.5) * mm, "end": v(170.56, 0.5) * mm});
            skArc(sketch, "E38.42.18.0", {"start": v(180.35, -11.4) * mm, "mid": v(174.67, -14.49) * mm, "end": v(170.56, -9.5) * mm});
            skCircle(sketch, "E38.46.18.0", {"center": v(186.35, -15.4) * mm, "radius": 2 * mm});
            skCircle(sketch, "E38.48.18.0", {"center": v(186.35, 16.4) * mm, "radius": 2 * mm});
            skCircle(sketch, "E38.50.18.0", {"center": v(230.97, -15.4) * mm, "radius": 2 * mm});
            skCircle(sketch, "E38.52.18.0", {"center": v(230.97, 16.4) * mm, "radius": 2 * mm});
            skArc(sketch, "E38.3.19.0", {"start": v(255.48, 78.02) * mm, "mid": v(242.1, 84.93) * mm, "end": v(233.28, 97.13) * mm});
            skArc(sketch, "E38.4.19.0", {"start": v(260.01, 61.11) * mm, "mid": v(251.88, 48.44) * mm, "end": v(250.34, 33.46) * mm});
            skArc(sketch, "E38.8.19.0", {"start": v(260.01, 61.11) * mm, "mid": v(262.73, 70.9) * mm, "end": v(255.48, 78.02) * mm});
            skArc(sketch, "E38.12.19.0", {"start": v(235.76, 74.03) * mm, "mid": v(230.5, 77.78) * mm, "end": v(225.81, 73.33) * mm});
            skLineSegment(sketch, "E38.16.19.0", {"start": v(235.76, 74.03) * mm, "end": v(238.35, 64.37) * mm});
            skLineSegment(sketch, "E38.19.19.0", {"start": v(240.94, 54.7) * mm, "end": v(238.35, 64.37) * mm});
            skArc(sketch, "E38.22.19.0", {"start": v(240.94, 54.7) * mm, "mid": v(238.26, 48.83) * mm, "end": v(231.98, 50.33) * mm});
            skLineSegment(sketch, "E38.26.19.0", {"start": v(231.98, 50.33) * mm, "end": v(177.28, 35.68) * mm});
            skLineSegment(sketch, "E38.29.19.0", {"start": v(225.81, 73.33) * mm, "end": v(171.12, 58.68) * mm});
            skArc(sketch, "E38.32.19.0", {"start": v(171.12, 58.68) * mm, "mid": v(164.84, 60.19) * mm, "end": v(162.16, 54.3) * mm});
            skLineSegment(sketch, "E38.36.19.0", {"start": v(162.16, 54.3) * mm, "end": v(164.75, 44.65) * mm});
            skLineSegment(sketch, "E38.39.19.0", {"start": v(167.34, 34.98) * mm, "end": v(164.75, 44.65) * mm});
            skArc(sketch, "E38.42.19.0", {"start": v(177.28, 35.68) * mm, "mid": v(172.6, 31.23) * mm, "end": v(167.34, 34.98) * mm});
            skCircle(sketch, "E38.46.19.0", {"center": v(184.11, 33.37) * mm, "radius": 2 * mm});
            skCircle(sketch, "E38.48.19.0", {"center": v(175.88, 64.1) * mm, "radius": 2 * mm});
            skCircle(sketch, "E38.50.19.0", {"center": v(227.22, 44.92) * mm, "radius": 2 * mm});
            skCircle(sketch, "E38.52.19.0", {"center": v(218.98, 75.65) * mm, "radius": 2 * mm});
            skArc(sketch, "E38.3.20.0", {"start": v(226.71, 141.5) * mm, "mid": v(212, 144.72) * mm, "end": v(200.32, 154.22) * mm});
            skArc(sketch, "E38.4.20.0", {"start": v(235.46, 126.34) * mm, "mid": v(230.9, 112) * mm, "end": v(233.28, 97.13) * mm});
            skArc(sketch, "E38.8.20.0", {"start": v(235.46, 126.34) * mm, "mid": v(235.56, 136.5) * mm, "end": v(226.71, 141.5) * mm});
            skArc(sketch, "E38.12.20.0", {"start": v(208.7, 132.54) * mm, "mid": v(202.65, 134.8) * mm, "end": v(199.27, 129.3) * mm});
            skLineSegment(sketch, "E38.16.20.0", {"start": v(208.7, 132.54) * mm, "end": v(213.7, 123.88) * mm});
            skLineSegment(sketch, "E38.19.20.0", {"start": v(218.7, 115.22) * mm, "end": v(213.7, 123.88) * mm});
            skArc(sketch, "E38.22.20.0", {"start": v(218.7, 115.22) * mm, "mid": v(217.63, 108.85) * mm, "end": v(211.17, 108.68) * mm});
            skLineSegment(sketch, "E38.26.20.0", {"start": v(211.17, 108.68) * mm, "end": v(162.14, 80.36) * mm});
            skLineSegment(sketch, "E38.29.20.0", {"start": v(199.27, 129.3) * mm, "end": v(150.23, 100.99) * mm});
            skArc(sketch, "E38.32.20.0", {"start": v(150.23, 100.99) * mm, "mid": v(143.77, 100.82) * mm, "end": v(142.7, 94.44) * mm});
            skLineSegment(sketch, "E38.36.20.0", {"start": v(142.7, 94.44) * mm, "end": v(147.7, 85.78) * mm});
            skLineSegment(sketch, "E38.39.20.0", {"start": v(152.7, 77.12) * mm, "end": v(147.7, 85.78) * mm});
            skArc(sketch, "E38.42.20.0", {"start": v(162.14, 80.36) * mm, "mid": v(158.76, 74.86) * mm, "end": v(152.7, 77.12) * mm});
            skCircle(sketch, "E38.46.20.0", {"center": v(169.33, 79.9) * mm, "radius": 2 * mm});
            skCircle(sketch, "E38.48.20.0", {"center": v(153.43, 107.45) * mm, "radius": 2 * mm});
            skCircle(sketch, "E38.50.20.0", {"center": v(207.98, 102.21) * mm, "radius": 2 * mm});
            skCircle(sketch, "E38.52.20.0", {"center": v(192.07, 129.76) * mm, "radius": 2 * mm});
            skArc(sketch, "E38.3.21.0", {"start": v(182.5, 195.37) * mm, "mid": v(167.46, 194.67) * mm, "end": v(153.71, 200.83) * mm});
            skArc(sketch, "E38.4.21.0", {"start": v(194.87, 183) * mm, "mid": v(194.17, 167.96) * mm, "end": v(200.32, 154.22) * mm});
            skArc(sketch, "E38.8.21.0", {"start": v(194.87, 183) * mm, "mid": v(192.33, 192.83) * mm, "end": v(182.5, 195.37) * mm});
            skArc(sketch, "E38.12.21.0", {"start": v(167.41, 182.06) * mm, "mid": v(160.98, 182.68) * mm, "end": v(159.14, 176.48) * mm});
            skLineSegment(sketch, "E38.16.21.0", {"start": v(167.41, 182.06) * mm, "end": v(174.48, 174.99) * mm});
            skLineSegment(sketch, "E38.19.21.0", {"start": v(181.56, 167.91) * mm, "end": v(174.48, 174.99) * mm});
            skArc(sketch, "E38.22.21.0", {"start": v(181.56, 167.91) * mm, "mid": v(182.18, 161.48) * mm, "end": v(175.98, 159.65) * mm});
            skLineSegment(sketch, "E38.26.21.0", {"start": v(175.98, 159.65) * mm, "end": v(135.94, 119.6) * mm});
            skLineSegment(sketch, "E38.29.21.0", {"start": v(159.14, 176.48) * mm, "end": v(119.1, 136.45) * mm});
            skArc(sketch, "E38.32.21.0", {"start": v(119.1, 136.45) * mm, "mid": v(112.91, 134.6) * mm, "end": v(113.53, 128.18) * mm});
            skLineSegment(sketch, "E38.36.21.0", {"start": v(113.53, 128.18) * mm, "end": v(120.6, 121.1) * mm});
            skLineSegment(sketch, "E38.39.21.0", {"start": v(127.67, 114.03) * mm, "end": v(120.6, 121.1) * mm});
            skArc(sketch, "E38.42.21.0", {"start": v(135.94, 119.6) * mm, "mid": v(134.1, 113.41) * mm, "end": v(127.67, 114.03) * mm});
            skCircle(sketch, "E38.46.21.0", {"center": v(143.02, 121.02) * mm, "radius": 2 * mm});
            skCircle(sketch, "E38.48.21.0", {"center": v(120.52, 143.52) * mm, "radius": 2 * mm});
            skCircle(sketch, "E38.50.21.0", {"center": v(174.57, 152.57) * mm, "radius": 2 * mm});
            skCircle(sketch, "E38.52.21.0", {"center": v(152.07, 175.07) * mm, "radius": 2 * mm});
            skArc(sketch, "E38.3.22.0", {"start": v(125.84, 235.97) * mm, "mid": v(111.5, 231.4) * mm, "end": v(96.63, 233.78) * mm});
            skArc(sketch, "E38.4.22.0", {"start": v(141, 227.21) * mm, "mid": v(144.21, 212.5) * mm, "end": v(153.71, 200.83) * mm});
            skArc(sketch, "E38.8.22.0", {"start": v(141, 227.21) * mm, "mid": v(136, 236.06) * mm, "end": v(125.84, 235.97) * mm});
            skArc(sketch, "E38.12.22.0", {"start": v(114.72, 219.2) * mm, "mid": v(108.34, 218.14) * mm, "end": v(108.17, 211.68) * mm});
            skLineSegment(sketch, "E38.16.22.0", {"start": v(114.72, 219.2) * mm, "end": v(123.38, 214.2) * mm});
            skLineSegment(sketch, "E38.19.22.0", {"start": v(132.04, 209.2) * mm, "end": v(123.38, 214.2) * mm});
            skArc(sketch, "E38.22.22.0", {"start": v(132.04, 209.2) * mm, "mid": v(134.3, 203.15) * mm, "end": v(128.8, 199.77) * mm});
            skLineSegment(sketch, "E38.26.22.0", {"start": v(128.8, 199.77) * mm, "end": v(100.48, 150.73) * mm});
            skLineSegment(sketch, "E38.29.22.0", {"start": v(108.17, 211.68) * mm, "end": v(79.86, 162.64) * mm});
            skArc(sketch, "E38.32.22.0", {"start": v(79.86, 162.64) * mm, "mid": v(74.35, 159.26) * mm, "end": v(76.62, 153.21) * mm});
            skLineSegment(sketch, "E38.36.22.0", {"start": v(76.62, 153.21) * mm, "end": v(85.28, 148.2) * mm});
            skLineSegment(sketch, "E38.39.22.0", {"start": v(93.94, 143.2) * mm, "end": v(85.28, 148.2) * mm});
            skArc(sketch, "E38.42.22.0", {"start": v(100.48, 150.73) * mm, "mid": v(100.31, 144.27) * mm, "end": v(93.94, 143.2) * mm});
            skCircle(sketch, "E38.46.22.0", {"center": v(106.95, 153.93) * mm, "radius": 2 * mm});
            skCircle(sketch, "E38.48.22.0", {"center": v(79.4, 169.84) * mm, "radius": 2 * mm});
            skCircle(sketch, "E38.50.22.0", {"center": v(129.26, 192.57) * mm, "radius": 2 * mm});
            skCircle(sketch, "E38.52.22.0", {"center": v(101.7, 208.48) * mm, "radius": 2 * mm});
            skArc(sketch, "E38.3.23.0", {"start": v(60.6, 260.51) * mm, "mid": v(47.93, 252.39) * mm, "end": v(32.96, 250.84) * mm});
            skArc(sketch, "E38.4.23.0", {"start": v(77.52, 255.98) * mm, "mid": v(84.43, 242.6) * mm, "end": v(96.63, 233.78) * mm});
            skArc(sketch, "E38.8.23.0", {"start": v(77.52, 255.98) * mm, "mid": v(70.4, 263.23) * mm, "end": v(60.6, 260.51) * mm});
            skArc(sketch, "E38.12.23.0", {"start": v(54.2, 241.44) * mm, "mid": v(48.33, 238.76) * mm, "end": v(49.83, 232.48) * mm});
            skLineSegment(sketch, "E38.16.23.0", {"start": v(54.2, 241.44) * mm, "end": v(63.87, 238.85) * mm});
            skLineSegment(sketch, "E38.19.23.0", {"start": v(73.53, 236.26) * mm, "end": v(63.87, 238.85) * mm});
            skArc(sketch, "E38.22.23.0", {"start": v(73.53, 236.26) * mm, "mid": v(77.28, 231) * mm, "end": v(72.83, 226.31) * mm});
            skLineSegment(sketch, "E38.26.23.0", {"start": v(72.83, 226.31) * mm, "end": v(58.18, 171.62) * mm});
            skLineSegment(sketch, "E38.29.23.0", {"start": v(49.83, 232.48) * mm, "end": v(35.18, 177.79) * mm});
            skArc(sketch, "E38.32.23.0", {"start": v(35.18, 177.79) * mm, "mid": v(30.73, 173.1) * mm, "end": v(34.48, 167.84) * mm});
            skLineSegment(sketch, "E38.36.23.0", {"start": v(34.48, 167.84) * mm, "end": v(44.14, 165.25) * mm});
            skLineSegment(sketch, "E38.39.23.0", {"start": v(53.8, 162.66) * mm, "end": v(44.14, 165.25) * mm});
            skArc(sketch, "E38.42.23.0", {"start": v(58.18, 171.62) * mm, "mid": v(59.68, 165.34) * mm, "end": v(53.8, 162.66) * mm});
            skCircle(sketch, "E38.46.23.0", {"center": v(63.6, 176.38) * mm, "radius": 2 * mm});
            skCircle(sketch, "E38.48.23.0", {"center": v(32.87, 184.62) * mm, "radius": 2 * mm});
            skCircle(sketch, "E38.50.23.0", {"center": v(75.14, 219.48) * mm, "radius": 2 * mm});
            skCircle(sketch, "E38.52.23.0", {"center": v(44.41, 227.72) * mm, "radius": 2 * mm});
            skSolve(sketch);
        }
        {
            var Q0;
            Q0 = qSketchRegion(id + "F0", true);
            extrude(context, id + "F1", {"entities" : qUnion([Q0]), "depth" : 25 * mm, "offsetDistance" : 25 * mm});
        }
        {
            var Q0;
            Q0 = qSketchRegion(id + "F0", true);
            extrude(context, id + "F2", {"entities" : qUnion([Q0]), "operationType" : NewBodyOperationType.ADD, "depth" : 25 * mm, "offsetDistance" : 25 * mm});
        }
    });
